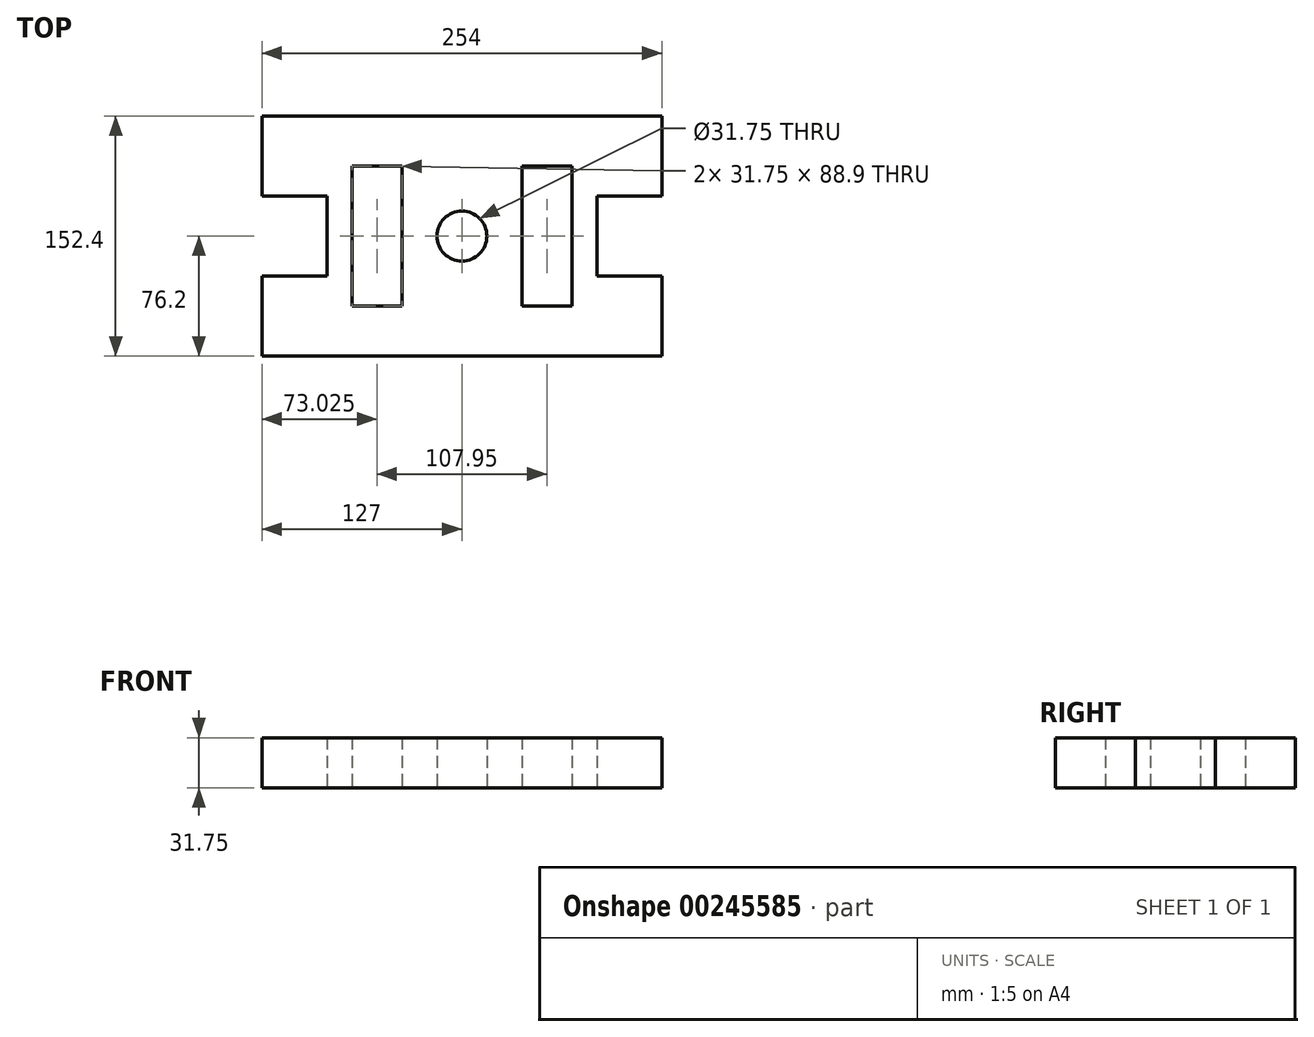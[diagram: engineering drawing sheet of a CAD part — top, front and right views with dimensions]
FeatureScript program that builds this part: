
annotation { "Feature Type Name" : "Feature", "Feature Type Description" : "" }
export const myFeature = defineFeature(function(context is Context, id is Id, definition is map)
    precondition{}
    {
        {
            var Q0;
            Q0=qCreatedBy(makeId("Top.planeOp"),FACE);
            var sketch = newSketch(context, id + "F0", { "sketchPlane" : qUnion([Q0])});
            skLineSegment(sketch, "E0.bottom", {"start": v(127, -76.2) * mm, "end": v(-127, -76.2) * mm});
            skLineSegment(sketch, "E0.top", {"start": v(127, 76.2) * mm, "end": v(-127, 76.2) * mm});
            skLineSegment(sketch, "E0.left", {"start": v(127, -76.2) * mm, "end": v(127, -25.4) * mm});
            skLineSegment(sketch, "E0.right", {"start": v(-127, -76.2) * mm, "end": v(-127, -25.4) * mm});
            skPoint(sketch, "E0.middle", {"position": v(0, 0) * mm});
            skCircle(sketch, "E1", {"center": v(0, 0) * mm, "radius": 15.88 * mm});
            skLineSegment(sketch, "E2.bottom", {"start": v(-127, 25.4) * mm, "end": v(-85.72, 25.4) * mm});
            skLineSegment(sketch, "E2.top", {"start": v(-127, -25.4) * mm, "end": v(-85.72, -25.4) * mm});
            skLineSegment(sketch, "E2.right", {"start": v(-85.72, 25.4) * mm, "end": v(-85.72, -25.4) * mm});
            skPoint(sketch, "E3.oppositeSnap0", {"position": v(-106.36, 25.4) * mm});
            skLineSegment(sketch, "E3.bottom", {"start": v(-106.36, 25.4) * mm, "end": v(-106.36, 25.4) * mm});
            skLineSegment(sketch, "E3.top", {"start": v(-106.36, 76.2) * mm, "end": v(-106.36, 76.2) * mm});
            skPoint(sketch, "E4.oppositeSnap0", {"position": v(-106.36, -25.4) * mm});
            skLineSegment(sketch, "E4.bottom", {"start": v(-106.36, -25.4) * mm, "end": v(-106.36, -25.4) * mm});
            skLineSegment(sketch, "E4.top", {"start": v(-106.36, -76.2) * mm, "end": v(-106.36, -76.2) * mm});
            skLineSegment(sketch, "E5.trimOffspring", {"start": v(-127, 25.4) * mm, "end": v(-127, 76.2) * mm});
            skLineSegment(sketch, "E6.bottom", {"start": v(127, 25.4) * mm, "end": v(85.73, 25.4) * mm});
            skLineSegment(sketch, "E6.top", {"start": v(127, -25.4) * mm, "end": v(85.73, -25.4) * mm});
            skLineSegment(sketch, "E6.right", {"start": v(85.72, 25.4) * mm, "end": v(85.72, -25.4) * mm});
            skPoint(sketch, "E7.oppositeSnap0", {"position": v(106.36, 25.4) * mm});
            skLineSegment(sketch, "E7.bottom", {"start": v(106.36, 25.4) * mm, "end": v(106.36, 25.4) * mm});
            skLineSegment(sketch, "E7.top", {"start": v(106.36, 76.2) * mm, "end": v(106.36, 76.2) * mm});
            skPoint(sketch, "E8.oppositeSnap0", {"position": v(106.36, -25.4) * mm});
            skLineSegment(sketch, "E8.bottom", {"start": v(106.36, -25.4) * mm, "end": v(112.31, -25.4) * mm});
            skLineSegment(sketch, "E9.trimOffspring", {"start": v(127, 25.4) * mm, "end": v(127, 76.2) * mm});
            skPoint(sketch, "E10.end.orphan", {"position": v(127, 0) * mm});
            skPoint(sketch, "E10.start.orphan", {"position": v(85.73, 0) * mm});
            skPoint(sketch, "E11", {"position": v(69.85, 76.2) * mm});
            skLineSegment(sketch, "E12", {"start": v(69.85, -76.2) * mm, "end": v(69.85, 76.2) * mm});
            skLineSegment(sketch, "E13", {"start": v(-69.85, 76.2) * mm, "end": v(-69.85, -76.2) * mm});
            skPoint(sketch, "E14", {"position": v(-127, 50.8) * mm});
            skLineSegment(sketch, "E15", {"start": v(-38.1, 76.2) * mm, "end": v(-38.1, -76.2) * mm});
            skLineSegment(sketch, "E16", {"start": v(38.1, 76.2) * mm, "end": v(38.1, -76.2) * mm});
            skLineSegment(sketch, "E17", {"start": v(-69.85, 44.45) * mm, "end": v(-38.1, 44.45) * mm});
            skLineSegment(sketch, "E18", {"start": v(-69.85, -44.45) * mm, "end": v(-38.1, -44.45) * mm});
            skLineSegment(sketch, "E19", {"start": v(38.1, -44.45) * mm, "end": v(69.85, -44.45) * mm});
            skLineSegment(sketch, "E20", {"start": v(38.1, 44.45) * mm, "end": v(69.85, 44.45) * mm});
            skSolve(sketch);
        }
        {
            var Q0;
            Q0 = qSketchRegion(id + "F0", true);
            extrude(context, id + "F1", {"entities" : qUnion([Q0]), "depth" : 31.75 * mm});
        }
    });
